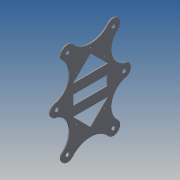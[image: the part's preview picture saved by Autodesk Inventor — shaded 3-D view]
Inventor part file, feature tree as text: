
AUTODESK INVENTOR PART (.ipt)
format: ipt  version: 2014 (Build 180170000, 170)  size: 187,904 bytes
history: native  units: mm
features: extrude x1, sketch x1
ambient origin geometry x8: Origin, YZ Plane, XZ Plane, XY Plane, X Axis, Y Axis, Z Axis, Center Point
bodies: Solid1 (feature_tree)
feature tree (2):
  extrude  "Extrusion1"  Depth=2.0mm TaperAngle=0.0deg
  sketch  "Sketch1"  dims[d0=165.0mm d1=85.5mm d2=82.5mm d3=20.0mm d4=20.0mm d5=25.0mm d6=25.0mm d7=25.0mm d8=25.0mm d9=25.0mm d10=25.0mm d11=7.0mm d12=7.0mm d13=7.0mm d14=7.0mm d15=7.0mm d16=7.0mm d17=45.0deg d18=45.0deg d19=45.0deg d20=45.0deg d21=45.0deg d22=45.0deg d23=45.0deg d24=90.0deg d26=16.0mm d27=11.0mm d28=11.0mm d29=150.67767mm d30=61.6967mm d31=63.5mm d32=18.0mm d33=73.282503mm d34=31.0mm d35=46.0mm d36=46.0mm d37=65.053824mm d38=18.0mm d39=65.0mm d40=46.0mm d41=46.0mm d42=18.0mm d43=2.0mm d44=6.5mm d45=2.0mm d46=2.0mm d47=33.0mm d48=17.0mm d49=17.0mm d50=33.0mm d51=2.0mm d52=2.0mm d53=33.0mm d54=33.0mm d55=17.0mm d56=17.0mm d57=2.0mm d58=0.0mm]
